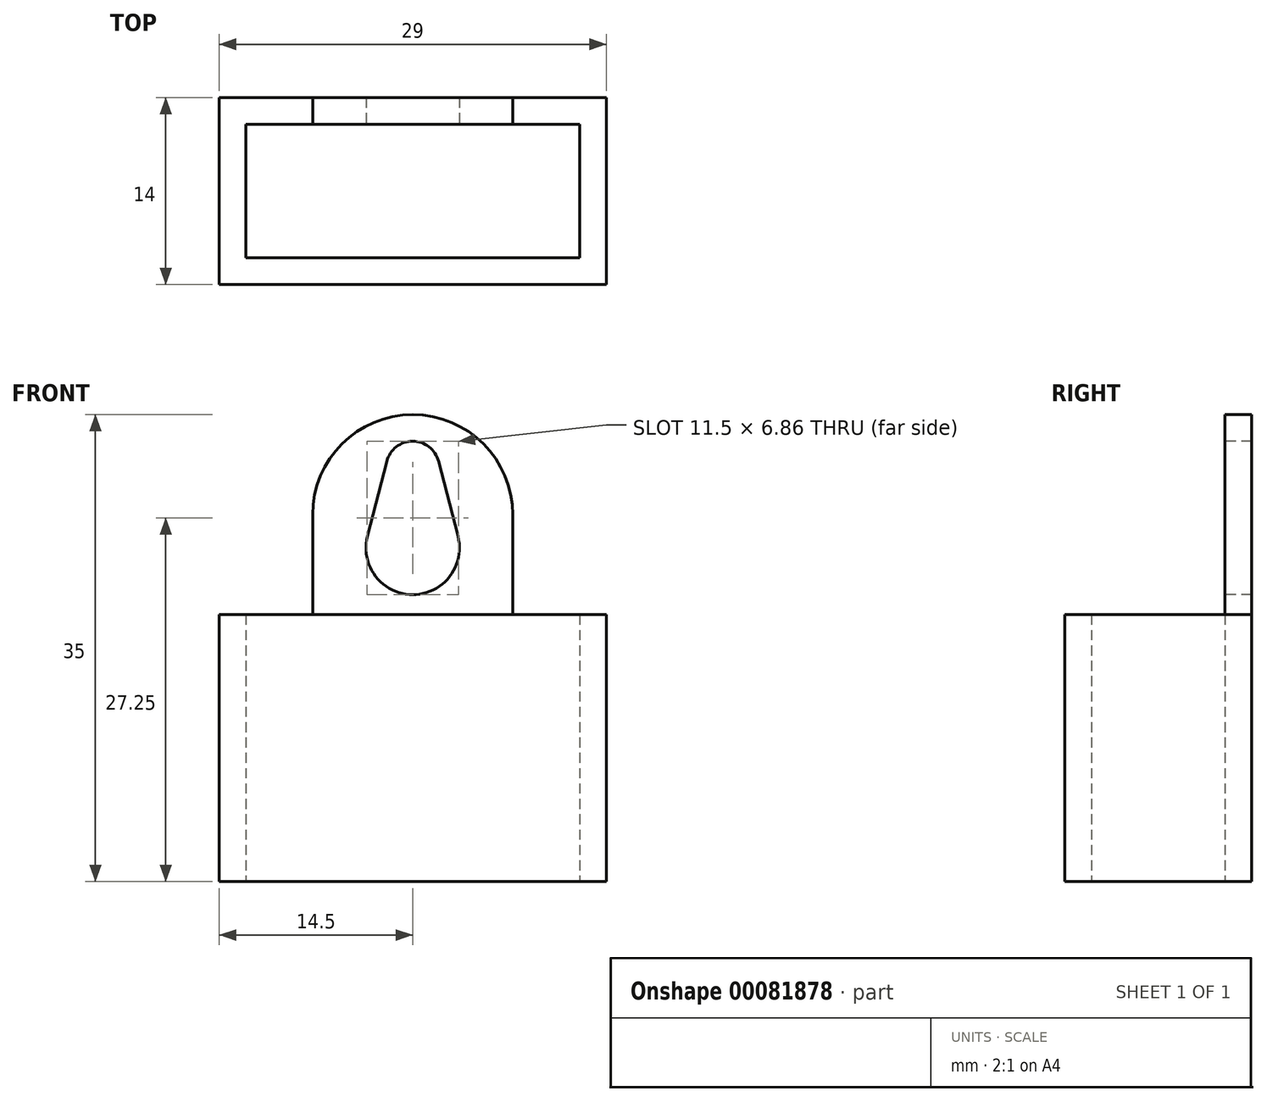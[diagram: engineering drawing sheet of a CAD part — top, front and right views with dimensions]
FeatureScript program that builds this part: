
annotation { "Feature Type Name" : "Feature", "Feature Type Description" : "" }
export const myFeature = defineFeature(function(context is Context, id is Id, definition is map)
    precondition{}
    {
        {
            var Q0;
            Q0=qCreatedBy(makeId("Top.planeOp"),FACE);
            var sketch = newSketch(context, id + "F0", { "sketchPlane" : qUnion([Q0])});
            skLineSegment(sketch, "E0.bottom", {"start": v(0, 0) * mm, "end": v(29, 0) * mm});
            skLineSegment(sketch, "E0.top", {"start": v(0, -14) * mm, "end": v(29, -14) * mm});
            skLineSegment(sketch, "E0.left", {"start": v(0, 0) * mm, "end": v(0, -14) * mm});
            skLineSegment(sketch, "E0.right", {"start": v(29, 0) * mm, "end": v(29, -14) * mm});
            skLineSegment(sketch, "E1.0", {"start": v(2, -2) * mm, "end": v(2, -12) * mm});
            skLineSegment(sketch, "E1.1", {"start": v(2, -2) * mm, "end": v(27, -2) * mm});
            skLineSegment(sketch, "E1.2", {"start": v(27, -2) * mm, "end": v(27, -12) * mm});
            skLineSegment(sketch, "E1.3", {"start": v(2, -12) * mm, "end": v(27, -12) * mm});
            skSolve(sketch);
        }
        {
            var Q0;
            Q0 = qSketchRegion(id + "F0", true);
            extrude(context, id + "F1", {"entities" : qUnion([Q0]), "depth" : 20 * mm});
        }
        {
            var Q0;
            Q0=makeQuery(id+"F1.opExtrude","CAP_FACE",FACE,{"disambiguationData":[OSD([sQuery(id+"F0.wireOp",EDGE,"E0.bottom"),sQuery(id+"F0.wireOp",EDGE,"E0.top"),sQuery(id+"F0.wireOp",EDGE,"E0.left"),sQuery(id+"F0.wireOp",EDGE,"E0.right"),sQuery(id+"F0.wireOp",EDGE,"E1.0"),sQuery(id+"F0.wireOp",EDGE,"E1.1"),sQuery(id+"F0.wireOp",EDGE,"E1.2"),sQuery(id+"F0.wireOp",EDGE,"E1.3")])],"isStart":false});
            var sketch = newSketch(context, id + "F2", { "sketchPlane" : qUnion([Q0])});
            skLineSegment(sketch, "E2.bottom", {"start": v(7, 0) * mm, "end": v(22, 0) * mm});
            skLineSegment(sketch, "E2.top", {"start": v(7, -2) * mm, "end": v(22, -2) * mm});
            skLineSegment(sketch, "E2.left", {"start": v(7, 0) * mm, "end": v(7, -2) * mm});
            skLineSegment(sketch, "E2.right", {"start": v(22, 0) * mm, "end": v(22, -2) * mm});
            skSolve(sketch);
        }
        {
            var Q0;
            Q0 = qSketchRegion(id + "F2", true);
            var Q1;
            Q1=sQuery(id+"F2.wireOp",EDGE,"E2.bottom");
            extrude(context, id + "F3", {"entities" : qUnion([Q0]), "operationType" : NewBodyOperationType.ADD, "surfaceEntities" : qUnion([Q1]), "depth" : 15 * mm});
        }
        {
            var Q0;
            Q0=makeQuery(id+"F3.boolean.opBoolean","MERGE",FACE,{"derivedFrom":[makeQuery(id+"F1.opExtrude","SWEPT_FACE",FACE,{"disambiguationData":[OSD([sQuery(id+"F0.wireOp",EDGE,"E1.1")])]}),makeQuery(id+"F3.opExtrude","SWEPT_FACE",FACE,{"disambiguationData":[OSD([sQuery(id+"F2.wireOp",EDGE,"E2.top")])]})]});
            var sketch = newSketch(context, id + "F4", { "sketchPlane" : qUnion([Q0])});
            skLineSegment(sketch, "E3", {"start": v(14.5, 35) * mm, "end": v(14.5, 20) * mm, "construction": true});
            skArc(sketch, "E4", {"start": v(16.44, 31.5) * mm, "mid": v(14.5, 33) * mm, "end": v(12.56, 31.5) * mm});
            skArc(sketch, "E5", {"start": v(11.11, 25.88) * mm, "mid": v(14.5, 21.5) * mm, "end": v(17.89, 25.88) * mm});
            skLineSegment(sketch, "E6", {"start": v(12.56, 31.5) * mm, "end": v(11.11, 25.88) * mm});
            skLineSegment(sketch, "E7", {"start": v(16.44, 31.5) * mm, "end": v(17.89, 25.88) * mm});
            skSolve(sketch);
        }
        {
            var Q0;
            Q0 = qSketchRegion(id + "F4", true);
            var Q1;
            Q1=makeQuery(id+"F3.boolean.opBoolean","MERGE",FACE,{"derivedFrom":[makeQuery(id+"F1.opExtrude","SWEPT_FACE",FACE,{"disambiguationData":[OSD([sQuery(id+"F0.wireOp",EDGE,"E0.bottom")])]}),makeQuery(id+"F3.opExtrude","SWEPT_FACE",FACE,{"disambiguationData":[OSD([sQuery(id+"F2.wireOp",EDGE,"E2.bottom")])]})]});
            extrude(context, id + "F5", {"entities" : qUnion([Q0]), "operationType" : NewBodyOperationType.REMOVE, "endBound" : BoundingType.UP_TO_SURFACE, "oppositeDirection" : true, "endBoundEntityFace" : qUnion([Q1]), "depth" : 25 * mm});
        }
        {
            var Q0;
            Q0=makeQuery(id+"F3.opExtrude","CAP_EDGE",EDGE,{"disambiguationData":[OSD([sQuery(id+"F2.wireOp",EDGE,"E2.left")])],"isStart":false});
            var Q1;
            Q1=makeQuery(id+"F3.opExtrude","CAP_EDGE",EDGE,{"disambiguationData":[OSD([sQuery(id+"F2.wireOp",EDGE,"E2.right")])],"isStart":false});
            var Q2;
            Q2=makeQuery(id+"F3.opExtrude","CAP_EDGE",EDGE,{"disambiguationData":[OSD([sQuery(id+"F2.wireOp",EDGE,"E2.right")])],"isStart":true});
            var Q3;
            Q3=makeQuery(id+"F3.opExtrude","CAP_EDGE",EDGE,{"disambiguationData":[OSD([sQuery(id+"F2.wireOp",EDGE,"E2.left")])],"isStart":true});
            fillet(context, id + "F6", {"entities" : qUnion([Q0, Q1, Q2, Q3]), "radius" : 7.5 * mm, "tangentPropagation" : true, "allowEdgeOverflow" : false});
        }
    });
